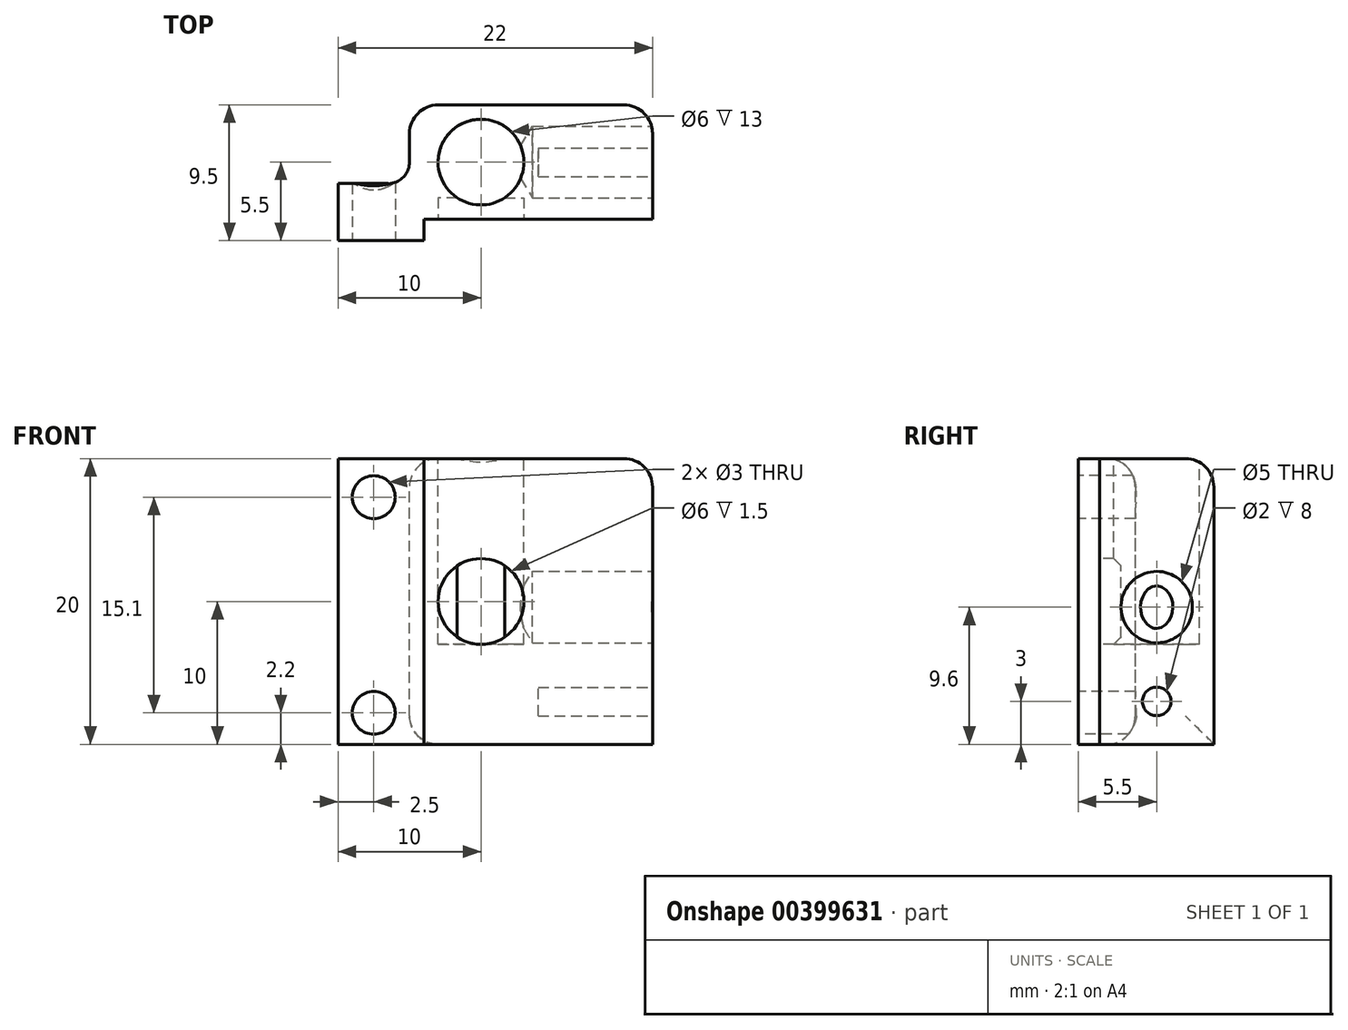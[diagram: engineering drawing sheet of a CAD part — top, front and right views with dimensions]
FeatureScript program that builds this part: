
annotation { "Feature Type Name" : "Feature", "Feature Type Description" : "" }
export const myFeature = defineFeature(function(context is Context, id is Id, definition is map)
    precondition{}
    {
        {
            var Q0;
            Q0=qCreatedBy(makeId("Top.planeOp"),FACE);
            var sketch = newSketch(context, id + "F0", { "sketchPlane" : qUnion([Q0])});
            skCircle(sketch, "E0", {"center": v(0, 0) * mm, "radius": 3 * mm});
            skLineSegment(sketch, "E1.bottom", {"start": v(-5, 4) * mm, "end": v(12, 4) * mm});
            skLineSegment(sketch, "E1.top", {"start": v(-4, -4) * mm, "end": v(12, -4) * mm});
            skLineSegment(sketch, "E1.left", {"start": v(-5, 4) * mm, "end": v(-5, 0) * mm});
            skLineSegment(sketch, "E1.right", {"start": v(12, 4) * mm, "end": v(12, -4) * mm});
            skLineSegment(sketch, "E2.bottom", {"start": v(-4, -5.5) * mm, "end": v(-10, -5.5) * mm});
            skLineSegment(sketch, "E2.top", {"start": v(-6.5, -1.5) * mm, "end": v(-10, -1.5) * mm});
            skLineSegment(sketch, "E2.left", {"start": v(-4, -5.5) * mm, "end": v(-4, -4) * mm});
            skLineSegment(sketch, "E2.right", {"start": v(-10, -5.5) * mm, "end": v(-10, -1.5) * mm});
            skLineSegment(sketch, "E3", {"start": v(-10, -1.5) * mm, "end": v(-10, 7.73) * mm, "construction": true});
            skLineSegment(sketch, "E4", {"start": v(-5, 4) * mm, "end": v(-14.37, 4) * mm, "construction": true});
            skArc(sketch, "E5", {"start": v(-6.5, -1.5) * mm, "mid": v(-5.44, -1.06) * mm, "end": v(-5, 0) * mm});
            skSolve(sketch);
        }
        {
            var Q0;
            Q0=makeQuery(id+"F0.imprint","IMPRINT",FACE,{"disambiguationData":[TD([[makeQuery(id+"F0.imprint","IMPRINT",EDGE,{"derivedFrom":sQuery(id+"F0.wireOp",EDGE,"E0")}),-1.0]])]});
            var Q1;
            Q1=makeQuery(id+"F0.imprint","IMPRINT",FACE,{"disambiguationData":[TD([[makeQuery(id+"F0.imprint","IMPRINT",EDGE,{"derivedFrom":sQuery(id+"F0.wireOp",EDGE,"E0")}),1.0]])]});
            extrude(context, id + "F1", {"entities" : qUnion([Q0, Q1]), "oppositeDirection" : true, "depth" : 7 * mm, "hasSecondDirection" : true, "secondDirectionOppositeDirection" : false, "secondDirectionDepth" : 13 * mm});
        }
        {
            var Q0;
            Q0=makeQuery(id+"F1.opExtrude","CAP_FACE",FACE,{"disambiguationData":[OSD([sQuery(id+"F0.wireOp",EDGE,"E1.bottom"),sQuery(id+"F0.wireOp",EDGE,"E1.top"),sQuery(id+"F0.wireOp",EDGE,"E1.left"),sQuery(id+"F0.wireOp",EDGE,"E1.right"),sQuery(id+"F0.wireOp",EDGE,"E2.bottom"),sQuery(id+"F0.wireOp",EDGE,"E2.top"),sQuery(id+"F0.wireOp",EDGE,"E2.left"),sQuery(id+"F0.wireOp",EDGE,"E2.right"),sQuery(id+"F0.wireOp",EDGE,"E5")])],"isStart":true});
            var sketch = newSketch(context, id + "F2", { "sketchPlane" : qUnion([Q0])});
            skCircle(sketch, "E6", {"center": v(0, 0) * mm, "radius": 3 * mm});
            skSolve(sketch);
        }
        {
            var Q0;
            Q0=qSketchRegion(id+"F2",true);
            extrude(context, id + "F3", {"entities" : qUnion([Q0]), "operationType" : NewBodyOperationType.REMOVE, "oppositeDirection" : true, "depth" : 13 * mm});
        }
        {
            var Q0;
            Q0=makeQuery(id+"F1.opExtrude","SWEPT_FACE",FACE,{"disambiguationData":[OSD([sQuery(id+"F0.wireOp",EDGE,"E1.top")])]});
            var sketch = newSketch(context, id + "F4", { "sketchPlane" : qUnion([Q0])});
            skCircle(sketch, "E7", {"center": v(0, 3) * mm, "radius": 3 * mm});
            skSolve(sketch);
        }
        {
            var Q0;
            Q0=makeQuery(id+"F4.imprint","IMPRINT",FACE,{"disambiguationData":[TD([[makeQuery(id+"F4.imprint","IMPRINT",EDGE,{"derivedFrom":sQuery(id+"F4.wireOp",EDGE,"E7")}),1.0]])]});
            extrude(context, id + "F5", {"entities" : qUnion([Q0]), "operationType" : NewBodyOperationType.REMOVE, "oppositeDirection" : true, "depth" : 1.5 * mm});
        }
        {
            var Q0;
            Q0=makeQuery(id+"F1.opExtrude","SWEPT_FACE",FACE,{"disambiguationData":[OSD([sQuery(id+"F0.wireOp",EDGE,"E1.right")])]});
            var sketch = newSketch(context, id + "F6", { "sketchPlane" : qUnion([Q0])});
            skCircle(sketch, "E8", {"center": v(0, 2.6) * mm, "radius": 2.6 * mm});
            skSolve(sketch);
        }
        {
            var Q0;
            Q0=sQuery(id+"F6.wireOp",VERTEX,"E8.center");
            var Q1;
            Q1=makeQuery(id+"F1.opExtrude","SWEPT_BODY",BODY,{"disambiguationData":[OSD([sQuery(id+"F0.wireOp",EDGE,"E1.bottom"),sQuery(id+"F0.wireOp",EDGE,"E1.top"),sQuery(id+"F0.wireOp",EDGE,"E1.left"),sQuery(id+"F0.wireOp",EDGE,"E1.right"),sQuery(id+"F0.wireOp",EDGE,"E2.bottom"),sQuery(id+"F0.wireOp",EDGE,"E2.top"),sQuery(id+"F0.wireOp",EDGE,"E2.left"),sQuery(id+"F0.wireOp",EDGE,"E2.right"),sQuery(id+"F0.wireOp",EDGE,"E5")])]});
            hole(context, id + "F7", {"style" : HoleStyle.SIMPLE, "endStyle" : HoleEndStyle.BLIND, "holeDiameter" : 5 * mm, "holeDepth" : 8.4 * mm, "tappedDepth" : 12 * mm, "tapClearance" : 3, "locations" : qUnion([Q0]), "scope" : qUnion([Q1])});
        }
        {
            var Q0;
            Q0=makeQuery(id+"F1.opExtrude","SWEPT_FACE",FACE,{"disambiguationData":[OSD([sQuery(id+"F0.wireOp",EDGE,"E1.right")])]});
            var sketch = newSketch(context, id + "F8", { "sketchPlane" : qUnion([Q0])});
            skCircle(sketch, "E9", {"center": v(0, -4) * mm, "radius": 1 * mm});
            skSolve(sketch);
        }
        {
            var Q0;
            Q0=makeQuery(id+"F8.imprint","IMPRINT",FACE,{"disambiguationData":[TD([[makeQuery(id+"F8.imprint","IMPRINT",EDGE,{"derivedFrom":sQuery(id+"F8.wireOp",EDGE,"E9")}),1.0]])]});
            extrude(context, id + "F9", {"entities" : qUnion([Q0]), "operationType" : NewBodyOperationType.REMOVE, "oppositeDirection" : true, "depth" : 8 * mm});
        }
        {
            var Q0;
            Q0=makeQuery(id+"F1.opExtrude","SWEPT_FACE",FACE,{"disambiguationData":[OSD([sQuery(id+"F0.wireOp",EDGE,"E2.bottom")])]});
            var sketch = newSketch(context, id + "F10", { "sketchPlane" : qUnion([Q0])});
            skLineSegment(sketch, "E10", {"start": v(-7.5, 12.59) * mm, "end": v(-7.5, -7) * mm, "construction": true});
            skLineSegment(sketch, "E11", {"start": v(0, 13) * mm, "end": v(0, -7.6) * mm, "construction": true});
            skCircle(sketch, "E12", {"center": v(-7.5, 10.3) * mm, "radius": 1.5 * mm});
            skCircle(sketch, "E13", {"center": v(-7.5, -4.8) * mm, "radius": 1.5 * mm});
            skSolve(sketch);
        }
        {
            var Q0;
            Q0=makeQuery(id+"F10.imprint","IMPRINT",FACE,{"disambiguationData":[TD([[makeQuery(id+"F10.imprint","IMPRINT",EDGE,{"derivedFrom":sQuery(id+"F10.wireOp",EDGE,"E12")}),1.0]])]});
            var Q1;
            Q1=makeQuery(id+"F10.imprint","IMPRINT",FACE,{"disambiguationData":[TD([[makeQuery(id+"F10.imprint","IMPRINT",EDGE,{"derivedFrom":sQuery(id+"F10.wireOp",EDGE,"E13")}),1.0]])]});
            extrude(context, id + "F11", {"entities" : qUnion([Q0, Q1]), "operationType" : NewBodyOperationType.REMOVE, "oppositeDirection" : true, "depth" : 5 * mm});
        }
        {
            var Q0;
            Q0=makeQuery(id+"F1.opExtrude","CAP_EDGE",EDGE,{"disambiguationData":[OSD([sQuery(id+"F0.wireOp",EDGE,"E1.bottom")])],"isStart":true});
            var Q1;
            Q1=makeQuery(id+"F1.opExtrude","CAP_EDGE",EDGE,{"disambiguationData":[OSD([sQuery(id+"F0.wireOp",EDGE,"E1.left")])],"isStart":true});
            var Q2;
            Q2=makeQuery(id+"F1.opExtrude","CAP_EDGE",EDGE,{"disambiguationData":[OSD([sQuery(id+"F0.wireOp",EDGE,"E1.left")])],"isStart":false});
            var Q3;
            Q3=makeQuery(id+"F1.opExtrude","SWEPT_EDGE",EDGE,{"disambiguationData":[OSD([sQuery(id+"F0.wireOp",EDGE,"E1.bottom"),sQuery(id+"F0.wireOp",EDGE,"E1.left")])]});
            var Q4;
            Q4=makeQuery(id+"F1.opExtrude","SWEPT_EDGE",EDGE,{"disambiguationData":[OSD([sQuery(id+"F0.wireOp",EDGE,"E1.bottom"),sQuery(id+"F0.wireOp",EDGE,"E1.right")])]});
            var Q5;
            Q5=makeQuery(id+"F1.opExtrude","CAP_EDGE",EDGE,{"disambiguationData":[OSD([sQuery(id+"F0.wireOp",EDGE,"E1.right")])],"isStart":true});
            fillet(context, id + "F12", {"entities" : qUnion([Q0, Q1, Q2, Q3, Q4, Q5]), "radius" : 2 * mm, "tangentPropagation" : true, "allowEdgeOverflow" : false});
        }
    });
